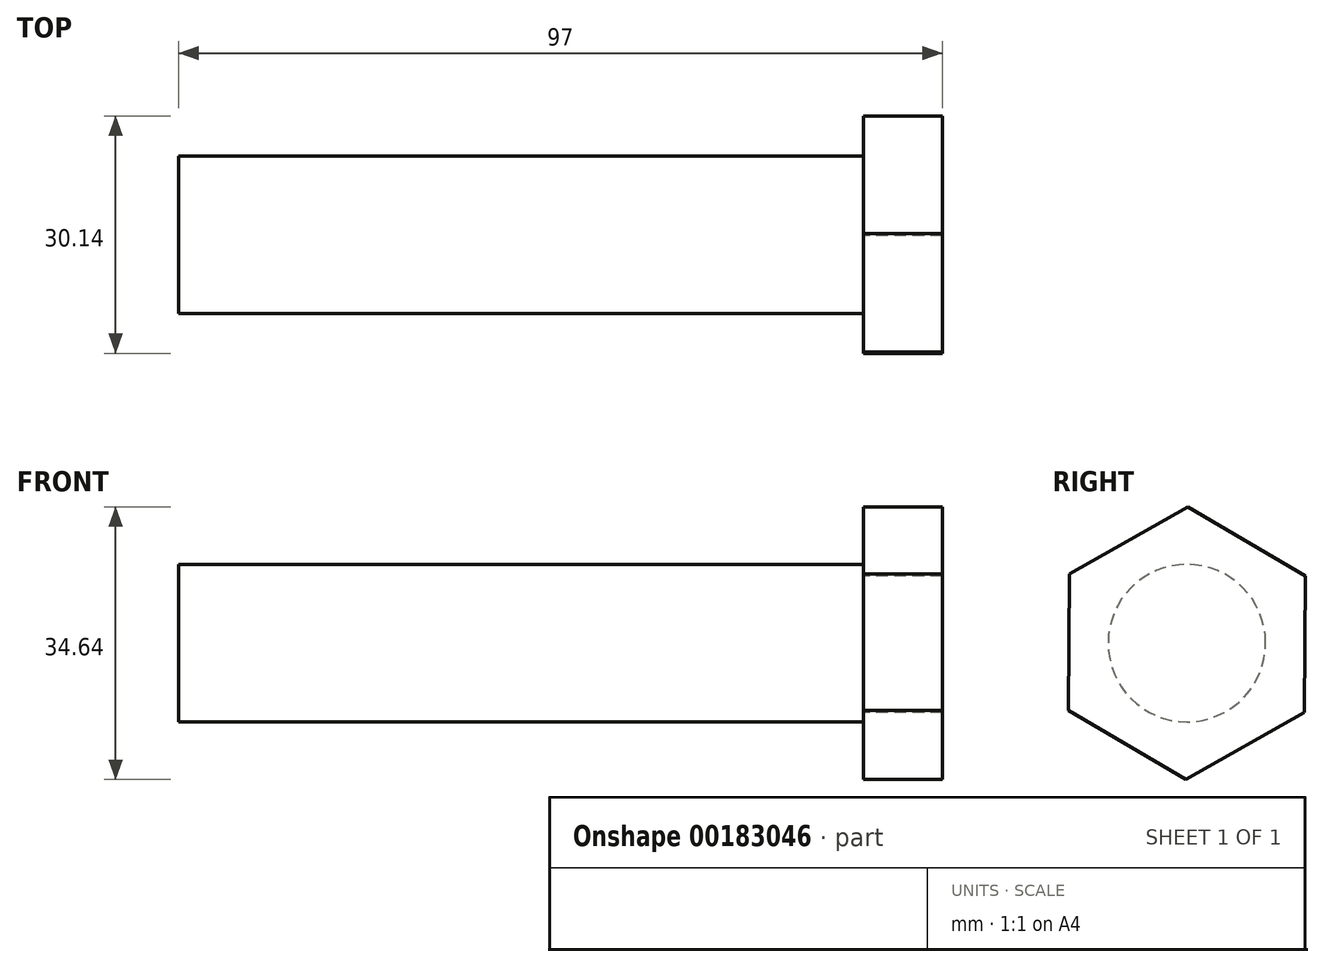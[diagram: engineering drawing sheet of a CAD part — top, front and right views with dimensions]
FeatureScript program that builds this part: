
annotation { "Feature Type Name" : "Feature", "Feature Type Description" : "" }
export const myFeature = defineFeature(function(context is Context, id is Id, definition is map)
    precondition{}
    {
        {
            var Q0;
            Q0=qCreatedBy(makeId("Right.planeOp"),FACE);
            var sketch = newSketch(context, id + "F0", { "sketchPlane" : qUnion([Q0])});
            skCircle(sketch, "E0", {"center": v(0, 0) * mm, "radius": 15 * mm});
            skCircle(sketch, "E1.cCircle", {"center": v(0, 0) * mm, "radius": 15 * mm, "construction": true});
            skLineSegment(sketch, "E1.0", {"start": v(0.14, 17.32) * mm, "end": v(15.07, 8.54) * mm});
            skLineSegment(sketch, "E1.1", {"start": v(15.07, 8.54) * mm, "end": v(14.93, -8.78) * mm});
            skLineSegment(sketch, "E1.2", {"start": v(14.93, -8.78) * mm, "end": v(-0.14, -17.32) * mm});
            skLineSegment(sketch, "E1.3", {"start": v(-0.14, -17.32) * mm, "end": v(-15.07, -8.54) * mm});
            skLineSegment(sketch, "E1.4", {"start": v(-15.07, -8.54) * mm, "end": v(-14.93, 8.78) * mm});
            skLineSegment(sketch, "E1.5", {"start": v(-14.93, 8.78) * mm, "end": v(0.14, 17.32) * mm});
            skPoint(sketch, "E1.0.midPoint", {"position": v(7.6, 12.93) * mm});
            skCircle(sketch, "E2", {"center": v(0, 0) * mm, "radius": 10 * mm});
            skSolve(sketch);
        }
        {
            var Q0;
            Q0=makeQuery(id+"F0.imprint","IMPRINT",FACE,{"disambiguationData":[TD([[makeQuery(id+"F0.imprint","IMPRINT",EDGE,{"derivedFrom":sQuery(id+"F0.wireOp",EDGE,"E2")}),1.0]])]});
            extrude(context, id + "F1", {"entities" : qUnion([Q0]), "oppositeDirection" : true, "depth" : 87 * mm});
        }
        {
            var Q0;
            Q0 = qSketchRegion(id + "F0", true);
            var Q1;
            Q1=makeQuery(id+"F1.opExtrude","CAP_FACE",FACE,{"disambiguationData":[OSD([sQuery(id+"F0.wireOp",EDGE,"E2")])],"isStart":true});
            extrude(context, id + "F2", {"entities" : qUnion([Q0, Q1]), "operationType" : NewBodyOperationType.ADD, "depth" : 10 * mm});
        }
    });
